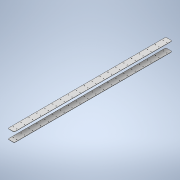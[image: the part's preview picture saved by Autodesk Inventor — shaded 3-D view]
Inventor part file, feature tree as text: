
AUTODESK INVENTOR PART (.ipt)
format: ipt  version: 2022 (Build 260153000, 153)  size: 243,712 bytes
history: native  units: mm
features: sketch x2, sheet_metal_op x1, chamfer x1, move_body x1, extrude x1, pattern_linear x1, mirror x1, other x1
ambient origin geometry x8: Origin, YZ Plane, XZ Plane, XY Plane, X Axis, Y Axis, Z Axis, Center Point
bodies: Solid1 (feature_tree)
feature tree (9):
  sheet_metal_op  "Face1"
  chamfer  "Corner Round1"
  move_body  "Move Body2"
  extrude  "Extrusion2"  Depth=40.0mm
  pattern_linear  "Rectangular Pattern1"  Spacing1=6.0mm  [1 undecoded]
  mirror  "Mirror2"
  sketch  "Sketch1"  dims[d0=1000.0mm d1=40.0mm]
  other  "Plate1"
  sketch  "Sketch3"  dims[d2=1.5mm d3=6.0mm d7=0.0mm d8=-30.0mm d9=0.0mm d10=20.0mm d11=11.0mm d12=3.35mm d13=25.0mm d19=9.0mm d20=25.0mm d21=3.35mm d22=10.0mm d23=0.0mm d24=200.0mm d26=50.0mm d27=20.0mm d29=22.0mm]
note: 1 required parameter value undecoded (feature->parameter linkage not recoverable at this tier; creation-order binding heuristic only, values carry confidence <= 0.55)
